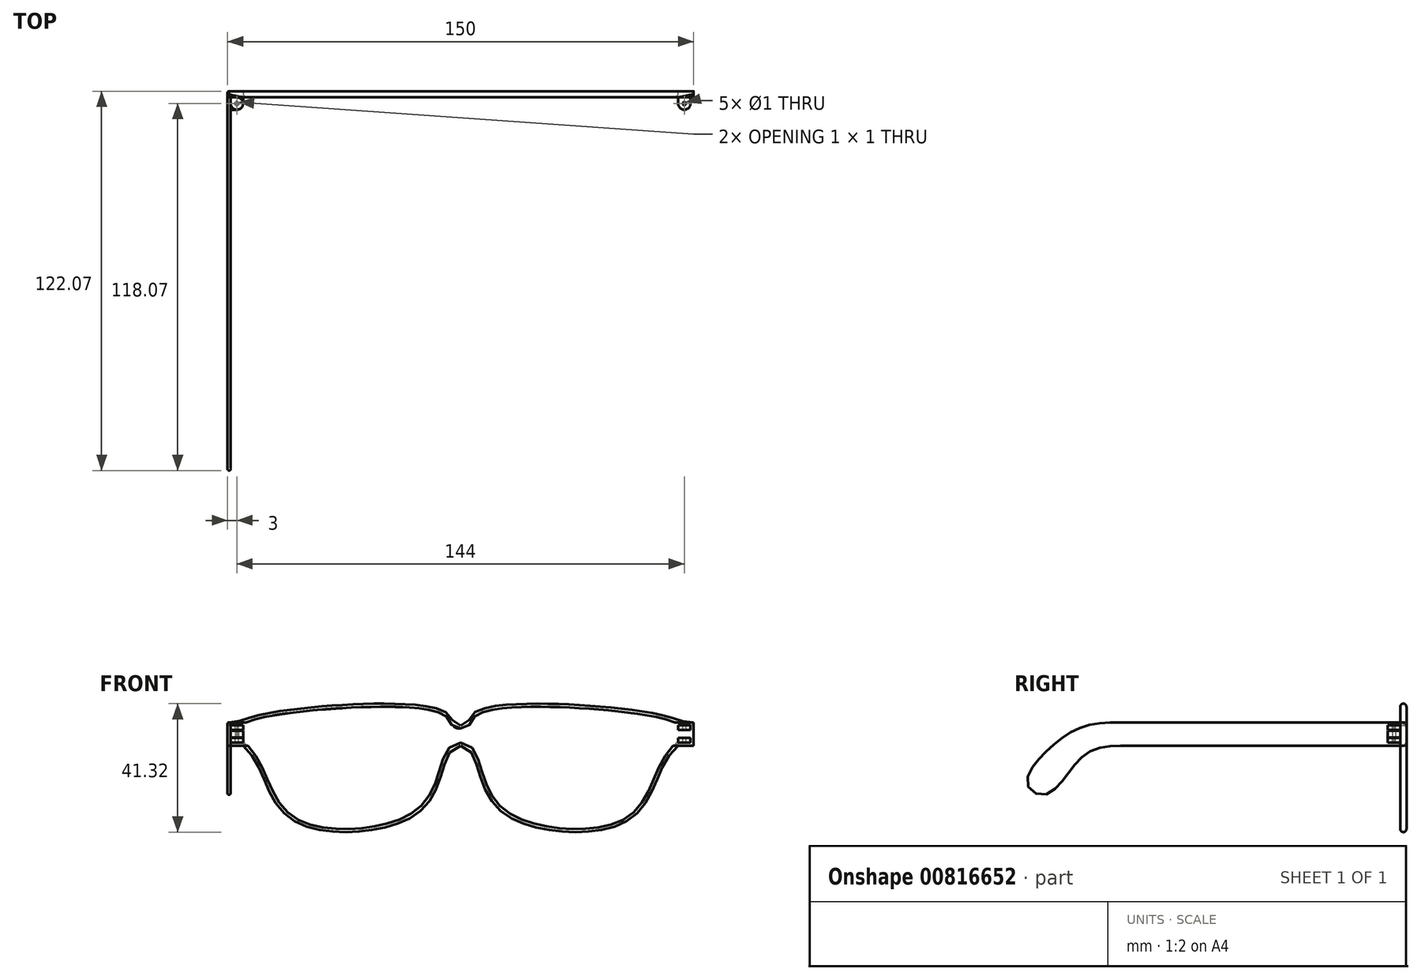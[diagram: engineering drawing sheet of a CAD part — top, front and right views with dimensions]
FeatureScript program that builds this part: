
annotation { "Feature Type Name" : "Feature", "Feature Type Description" : "" }
export const myFeature = defineFeature(function(context is Context, id is Id, definition is map)
    precondition{}
    {
        {
            var Q0;
            Q0=qCreatedBy(makeId("Front.planeOp"),FACE);
            var sketch = newSketch(context, id + "F0", { "sketchPlane" : qUnion([Q0])});
            skLineSegment(sketch, "E0", {"start": v(-75, -28.9) * mm, "end": v(-75, 32.7) * mm, "construction": true});
            skLineSegment(sketch, "E1", {"start": v(0, 0) * mm, "end": v(-4.56, 0) * mm, "construction": true});
            skLineSegment(sketch, "E2", {"start": v(-3.33, -24.15) * mm, "end": v(-65.98, -24.15) * mm, "construction": true});
            skLineSegment(sketch, "E3", {"start": v(-65.98, -24.15) * mm, "end": v(-64.31, 10) * mm, "construction": true});
            skLineSegment(sketch, "E4", {"start": v(-64.31, 10) * mm, "end": v(0, 10.78) * mm, "construction": true});
            skFitSpline(sketch, "E5", {"points": [v(0, 0) * mm, v(-4.25, -3.6) * mm, v(-7.5, -13.08) * mm, v(-18.05, -24.15) * mm, v(-53.68, -24.15) * mm, v(-65.12, -6.6) * mm, v(-69.95, 0) * mm, v(-75, 0) * mm], "startDerivative": vector(-72.74, 0) * mm, "endDerivative": vector(-133.49, 0) * mm});
            skFitSpline(sketch, "E6", {"points": [v(-75, 7.54) * mm, v(-64.31, 10) * mm, v(-4.56, 10.73) * mm, v(0, 6.53) * mm], "startDerivative": vector(58.2, 0) * mm, "endDerivative": vector(50.29, 0) * mm});
            skFitSpline(sketch, "E7.0", {"points": [v(-75, 4.04) * mm, v(-74.32, 4.04) * mm, v(-73.06, 4.09) * mm, v(-71.42, 4.29) * mm, v(-69.96, 4.62) * mm, v(-68.7, 5.01) * mm, v(-67.56, 5.41) * mm, v(-66.4, 5.81) * mm, v(-65.03, 6.23) * mm, v(-63.3, 6.66) * mm, v(-61.02, 7.11) * mm, v(-57.38, 7.72) * mm, v(-51.9, 8.44) * mm, v(-44.33, 9.2) * mm, v(-36.27, 9.76) * mm, v(-29.53, 10.02) * mm, v(-24.37, 10.06) * mm, v(-20.68, 10) * mm, v(-17.23, 9.86) * mm, v(-14.1, 9.61) * mm, v(-11.34, 9.26) * mm, v(-9.45, 8.9) * mm, v(-8.23, 8.56) * mm, v(-7.47, 8.3) * mm, v(-6.91, 8.07) * mm, v(-6.62, 7.9) * mm, v(-6.5, 7.82) * mm, v(-6.42, 7.75) * mm, v(-6.35, 7.67) * mm, v(-6.25, 7.54) * mm, v(-6.11, 7.31) * mm, v(-5.93, 6.95) * mm, v(-5.67, 6.43) * mm, v(-5.29, 5.75) * mm, v(-4.68, 4.92) * mm, v(-3.76, 4.07) * mm, v(-2.55, 3.42) * mm, v(-1.27, 3.09) * mm, v(-0.42, 3.03) * mm, v(0, 3.03) * mm]});
            skFitSpline(sketch, "E8.0", {"points": [v(0, 3.5) * mm, v(-0.65, 3.5) * mm, v(-1.95, 3.35) * mm, v(-3.73, 2.6) * mm, v(-5.14, 1.5) * mm, v(-6.17, 0.27) * mm, v(-6.78, -0.77) * mm, v(-7.2, -1.59) * mm, v(-7.46, -2.18) * mm, v(-7.7, -2.78) * mm, v(-8.02, -3.58) * mm, v(-8.37, -4.58) * mm, v(-8.75, -5.78) * mm, v(-9.24, -7.38) * mm, v(-9.85, -9.37) * mm, v(-10.67, -11.68) * mm, v(-11.65, -13.85) * mm, v(-12.88, -15.85) * mm, v(-14.45, -17.69) * mm, v(-16.16, -19.1) * mm, v(-17.87, -20.17) * mm, v(-19.1, -20.8) * mm, v(-20.2, -21.27) * mm, v(-21.36, -21.74) * mm, v(-22.96, -22.28) * mm, v(-25.04, -22.85) * mm, v(-28, -23.5) * mm, v(-31.98, -24.08) * mm, v(-36.9, -24.35) * mm, v(-40.92, -24.18) * mm, v(-43.96, -23.8) * mm, v(-46.11, -23.37) * mm, v(-48.11, -22.84) * mm, v(-49.91, -22.18) * mm, v(-51.23, -21.54) * mm, v(-52.16, -21) * mm, v(-53.03, -20.4) * mm, v(-54.01, -19.58) * mm, v(-55.44, -18.1) * mm, v(-56.97, -15.96) * mm, v(-58.51, -13) * mm, v(-59.65, -10.35) * mm, v(-60.56, -8.2) * mm, v(-61.14, -6.85) * mm, v(-61.62, -5.79) * mm, v(-62, -5) * mm, v(-62.4, -4.22) * mm, v(-62.95, -3.23) * mm, v(-63.64, -2.08) * mm, v(-64.48, -0.84) * mm, v(-65.3, 0.27) * mm, v(-65.97, 1.06) * mm, v(-66.5, 1.64) * mm, v(-66.9, 2.03) * mm, v(-67.32, 2.4) * mm, v(-67.76, 2.75) * mm, v(-68.26, 3.09) * mm, v(-68.95, 3.44) * mm, v(-69.78, 3.68) * mm, v(-70.55, 3.75) * mm, v(-71.12, 3.74) * mm, v(-71.56, 3.7) * mm, v(-71.94, 3.66) * mm, v(-72.47, 3.6) * mm, v(-73.32, 3.53) * mm, v(-74.36, 3.5) * mm, v(-75, 3.5) * mm]});
            skFitSpline(sketch, "E9", {"points": [v(-60.4, -8.59) * mm, v(-62.23, 5.12) * mm, v(-51.33, 8.47) * mm], "startDerivative": vector(-12.73, 32.46) * mm, "endDerivative": vector(25.15, 4.32) * mm});
            skLineSegment(sketch, "E10", {"start": v(0, 6.53) * mm, "end": v(0, 0) * mm});
            skLineSegment(sketch, "E11", {"start": v(-75, 7.54) * mm, "end": v(-75, 0) * mm});
            skPoint(sketch, "E12.2.internal.snap0", {"position": v(-65.14, -7.08) * mm});
            skFitSpline(sketch, "E12", {"points": [v(-13.23, 9.5) * mm, v(-8.44, 6.53) * mm, v(-9.15, -7.08) * mm], "startDerivative": vector(14.77, -3.56) * mm, "endDerivative": vector(-7.02, -20.16) * mm});
            skLineSegment(sketch, "E13", {"start": v(-7.5, -22.45) * mm, "end": v(-7.5, 12.5) * mm, "construction": true});
            skSolve(sketch);
        }
        {
            var Q0;
            {var subQ8=sQuery(id+"F0.wireOp",EDGE,"E6");Q0=makeQuery(id+"F0.imprint","IMPRINT",FACE,{"disambiguationData":[TD([[makeQuery(id+"F0.imprint","IMPRINT",EDGE,{"derivedFrom":subQ8}),-1.0]])]});}
            var Q1;
            {var subQ3=sQuery(id+"F0.wireOp",EDGE,"E9");Q1=makeQuery(id+"F0.imprint","IMPRINT",FACE,{"disambiguationData":[TD([[makeQuery(id+"F0.imprint","IMPRINT",EDGE,{"derivedFrom":subQ3}),1.0]])]});}
            var Q2;
            {var subQ7=sQuery(id+"F0.wireOp",EDGE,"E5");Q2=makeQuery(id+"F0.imprint","IMPRINT",FACE,{"disambiguationData":[TD([[makeQuery(id+"F0.imprint","IMPRINT",EDGE,{"derivedFrom":subQ7}),-1.0]])]});}
            var Q3;
            {var subQ0=sQuery(id+"F0.wireOp",EDGE,"E10");var subQ1=sQuery(id+"F0.wireOp",EDGE,"E7.0");var subQ2=makeQuery(id+"F0.imprint","INTERSECT",VERTEX,{"derivedFrom":[subQ1,subQ0]});Q3=makeQuery(id+"F0.imprint","IMPRINT",FACE,{"disambiguationData":[TD([[makeQuery(id+"F0.imprint","IMPRINT",EDGE,{"disambiguationData":[TD([[subQ2,1.0]])],"derivedFrom":subQ1}),-1.0]])]});}
            var Q4;
            {var subQ0=sQuery(id+"F0.wireOp",EDGE,"E12");var subQ1=sQuery(id+"F0.wireOp",EDGE,"E7.0");var subQ2=makeQuery(id+"F0.imprint","INTERSECT",VERTEX,{"disambiguationData":[OD(1.0)],"derivedFrom":[subQ1,subQ0]});Q4=makeQuery(id+"F0.imprint","IMPRINT",FACE,{"disambiguationData":[TD([[makeQuery(id+"F0.imprint","IMPRINT",EDGE,{"disambiguationData":[TD([[subQ2,-1.0]])],"derivedFrom":subQ1}),-1.0]])]});}
            var Q5;
            {var subQ0=sQuery(id+"F0.wireOp",EDGE,"E10");var subQ1=sQuery(id+"F0.wireOp",EDGE,"E7.0");var subQ2=makeQuery(id+"F0.imprint","INTERSECT",VERTEX,{"derivedFrom":[subQ1,subQ0]});Q5=makeQuery(id+"F0.imprint","IMPRINT",FACE,{"disambiguationData":[TD([[makeQuery(id+"F0.imprint","IMPRINT",EDGE,{"disambiguationData":[TD([[subQ2,1.0]])],"derivedFrom":subQ1}),1.0]])]});}
            extrude(context, id + "F1", {"entities" : qUnion([Q0, Q1, Q2, Q3, Q4, Q5]), "depth" : 2 * mm, "offsetDistance" : 25 * mm});
        }
        {
            var Q0;
            Q0=makeQuery(id+"F1.opExtrude","CAP_EDGE",EDGE,{"disambiguationData":[OSD([sQuery(id+"F0.wireOp",EDGE,"E5")])],"isStart":false});
            var Q1;
            Q1=makeQuery(id+"F1.opExtrude","CAP_EDGE",EDGE,{"disambiguationData":[OSD([sQuery(id+"F0.wireOp",EDGE,"E6")])],"isStart":false});
            var Q2;
            Q2=makeQuery(id+"F1.opExtrude","CAP_EDGE",EDGE,{"disambiguationData":[OSD([sQuery(id+"F0.wireOp",EDGE,"E5")])],"isStart":true});
            var Q3;
            Q3=makeQuery(id+"F1.opExtrude","CAP_EDGE",EDGE,{"disambiguationData":[OSD([sQuery(id+"F0.wireOp",EDGE,"E6")])],"isStart":true});
            fillet(context, id + "F2", {"entities" : qUnion([Q0, Q1, Q2, Q3]), "radius" : 1 * mm, "tangentPropagation" : true, "allowEdgeOverflow" : false});
        }
        {
            var Q0;
            Q0=makeQuery(id+"F1.opExtrude","SWEPT_FACE",FACE,{"disambiguationData":[OSD([sQuery(id+"F0.wireOp",EDGE,"E11")])]});
            var sketch = newSketch(context, id + "F3", { "sketchPlane" : qUnion([Q0])});
            skLineSegment(sketch, "E14", {"start": v(1, 7.54) * mm, "end": v(1, 0) * mm});
            skLineSegment(sketch, "E15", {"start": v(1, 0) * mm, "end": v(7.33, 0) * mm});
            skLineSegment(sketch, "E16", {"start": v(7.33, 0) * mm, "end": v(7.33, 7.54) * mm});
            skLineSegment(sketch, "E17", {"start": v(7.33, 7.54) * mm, "end": v(1, 7.54) * mm});
            skSolve(sketch);
        }
        {
            var Q0;
            Q0=makeQuery(id+"F3.imprint","IMPRINT",FACE,{"disambiguationData":[TD([[makeQuery(id+"F3.imprint","IMPRINT",EDGE,{"derivedFrom":sQuery(id+"F3.wireOp",EDGE,"E14")}),-1.0]])]});
            var Q1;
            Q1=makeQuery(id+"F3.imprint","IMPRINT",FACE,{"disambiguationData":[TD([[makeQuery(id+"F3.imprint","IMPRINT",EDGE,{"derivedFrom":sQuery(id+"F3.wireOp",EDGE,"E14")}),1.0]])]});
            var Q2;
            Q2=makeQuery(id+"F3.imprint","IMPRINT",FACE,{"disambiguationData":[TD([[makeQuery(id+"F3.imprint","IMPRINT",EDGE,{"derivedFrom":sQuery(id+"F3.wireOp",EDGE,"E15")}),1.0]])]});
            extrude(context, id + "F4", {"entities" : qUnion([Q0, Q1, Q2]), "operationType" : NewBodyOperationType.ADD, "oppositeDirection" : true, "depth" : 10 * mm, "offsetDistance" : 25 * mm});
        }
        {
            var Q0;
            Q0=makeQuery(id+"F4.opExtrude","SWEPT_FACE",FACE,{"disambiguationData":[OSD([sQuery(id+"F3.wireOp",EDGE,"E17")])]});
            var sketch = newSketch(context, id + "F5", { "sketchPlane" : qUnion([Q0])});
            skLineSegment(sketch, "E18", {"start": v(-65, -2) * mm, "end": v(-75, -2) * mm, "construction": true});
            skLineSegment(sketch, "E19", {"start": v(-75, -2) * mm, "end": v(-74, -2) * mm});
            skLineSegment(sketch, "E20", {"start": v(-74, -2) * mm, "end": v(-74, -4) * mm});
            skLineSegment(sketch, "E21", {"start": v(-74, -4) * mm, "end": v(-72, -4) * mm, "construction": true});
            skArc(sketch, "E22", {"start": v(-74, -4) * mm, "mid": v(-72, -6) * mm, "end": v(-70, -4) * mm});
            skLineSegment(sketch, "E23", {"start": v(-70, -4) * mm, "end": v(-70, -2) * mm});
            skCircle(sketch, "E24", {"center": v(-72, -4) * mm, "radius": 0.5 * mm});
            skLineSegment(sketch, "E25", {"start": v(-70, -2) * mm, "end": v(-69.05, -2) * mm});
            skSolve(sketch);
        }
        {
            var Q0;
            {var subQ8=sQuery(id+"F5.wireOp",EDGE,"E19");Q0=makeQuery(id+"F5.imprint","IMPRINT",FACE,{"disambiguationData":[TD([[makeQuery(id+"F5.imprint","IMPRINT",EDGE,{"derivedFrom":subQ8}),-1.0]])]});}
            var Q1;
            Q1=makeQuery(id+"F5.imprint","IMPRINT",FACE,{"disambiguationData":[TD([[makeQuery(id+"F5.imprint","IMPRINT",EDGE,{"derivedFrom":sQuery(id+"F5.wireOp",EDGE,"E24")}),1.0]])]});
            extrude(context, id + "F6", {"entities" : qUnion([Q0, Q1]), "operationType" : NewBodyOperationType.REMOVE, "oppositeDirection" : true, "depth" : 25 * mm, "offsetDistance" : 25 * mm});
        }
        {
            var Q0;
            Q0=makeQuery(id+"F6.boolean.opBoolean","COPY",FACE,{"derivedFrom":makeQuery(id+"F6.opExtrude","SWEPT_FACE",FACE,{"disambiguationData":[OSD([sQuery(id+"F5.wireOp",EDGE,"E20")])]})});
            var sketch = newSketch(context, id + "F7", { "sketchPlane" : qUnion([Q0])});
            skLineSegment(sketch, "E26", {"start": v(2, 7.54) * mm, "end": v(2, 6.54) * mm});
            skLineSegment(sketch, "E27", {"start": v(2, 6.54) * mm, "end": v(6.7, 6.54) * mm});
            skLineSegment(sketch, "E28", {"start": v(6.7, 6.54) * mm, "end": v(6.7, 5.04) * mm});
            skLineSegment(sketch, "E29", {"start": v(6.7, 5.04) * mm, "end": v(2, 5.04) * mm});
            skLineSegment(sketch, "E30", {"start": v(2, 5.04) * mm, "end": v(2, 2.5) * mm});
            skLineSegment(sketch, "E31", {"start": v(2, 2.5) * mm, "end": v(6.7, 2.5) * mm});
            skLineSegment(sketch, "E32", {"start": v(6.7, 2.5) * mm, "end": v(6.7, 1) * mm});
            skLineSegment(sketch, "E33", {"start": v(6.7, 1) * mm, "end": v(2, 1) * mm});
            skLineSegment(sketch, "E34", {"start": v(2, 1) * mm, "end": v(2, 0) * mm});
            skLineSegment(sketch, "E35", {"start": v(2, 7.54) * mm, "end": v(6.7, 7.54) * mm});
            skLineSegment(sketch, "E36", {"start": v(6.7, 7.54) * mm, "end": v(6.7, 6.54) * mm});
            skLineSegment(sketch, "E37", {"start": v(6.7, 5.04) * mm, "end": v(6.7, 2.5) * mm});
            skLineSegment(sketch, "E38", {"start": v(6.7, 1) * mm, "end": v(6.7, 0) * mm});
            skLineSegment(sketch, "E39", {"start": v(6.7, 0) * mm, "end": v(2, 0) * mm});
            skLineSegment(sketch, "E40", {"start": v(2, 1) * mm, "end": v(2, 2.5) * mm});
            skLineSegment(sketch, "E41", {"start": v(2, 5.04) * mm, "end": v(2, 6.54) * mm});
            skSolve(sketch);
        }
        {
            var Q0;
            {var subQ0=sQuery(id+"F7.wireOp",EDGE,"E36");Q0=makeQuery(id+"F7.imprint","IMPRINT",FACE,{"disambiguationData":[TD([[makeQuery(id+"F7.imprint","IMPRINT",EDGE,{"derivedFrom":subQ0}),-1.0]])]});}
            var Q1;
            {var subQ0=sQuery(id+"F7.wireOp",EDGE,"E26");Q1=makeQuery(id+"F7.imprint","IMPRINT",FACE,{"disambiguationData":[TD([[makeQuery(id+"F7.imprint","IMPRINT",EDGE,{"derivedFrom":subQ0}),-1.0]])]});}
            var Q2;
            {var subQ0=sQuery(id+"F7.wireOp",EDGE,"E30");Q2=makeQuery(id+"F7.imprint","IMPRINT",FACE,{"disambiguationData":[TD([[makeQuery(id+"F7.imprint","IMPRINT",EDGE,{"derivedFrom":subQ0}),-1.0]])]});}
            var Q3;
            {var subQ0=sQuery(id+"F7.wireOp",EDGE,"E37");Q3=makeQuery(id+"F7.imprint","IMPRINT",FACE,{"disambiguationData":[TD([[makeQuery(id+"F7.imprint","IMPRINT",EDGE,{"derivedFrom":subQ0}),-1.0]])]});}
            var Q4;
            {var subQ0=sQuery(id+"F7.wireOp",EDGE,"E38");Q4=makeQuery(id+"F7.imprint","IMPRINT",FACE,{"disambiguationData":[TD([[makeQuery(id+"F7.imprint","IMPRINT",EDGE,{"derivedFrom":subQ0}),-1.0]])]});}
            var Q5;
            {var subQ0=sQuery(id+"F7.wireOp",EDGE,"E34");Q5=makeQuery(id+"F7.imprint","IMPRINT",FACE,{"disambiguationData":[TD([[makeQuery(id+"F7.imprint","IMPRINT",EDGE,{"derivedFrom":subQ0}),-1.0]])]});}
            extrude(context, id + "F8", {"entities" : qUnion([Q0, Q1, Q2, Q3, Q4, Q5]), "operationType" : NewBodyOperationType.REMOVE, "oppositeDirection" : true, "depth" : 25 * mm, "offsetDistance" : 25 * mm});
        }
        {
            var Q0;
            {var subQ0=sQuery(id+"F0.wireOp",EDGE,"E11");Q0=makeQuery(id+"F4.boolean.opBoolean","MERGE",FACE,{"derivedFrom":[makeQuery(id+"F1.opExtrude","SWEPT_FACE",FACE,{"disambiguationData":[OSD([subQ0])]}),makeQuery(id+"F4.opExtrude","CAP_FACE",FACE,{"disambiguationData":[OSD([sQuery(id+"F0.wireOp",EDGE,"E5"),sQuery(id+"F0.wireOp",EDGE,"E6"),subQ0,sQuery(id+"F3.wireOp",EDGE,"E15"),sQuery(id+"F3.wireOp",EDGE,"E16"),sQuery(id+"F3.wireOp",EDGE,"E17")])],"isStart":true})]});}
            var sketch = newSketch(context, id + "F9", { "sketchPlane" : qUnion([Q0])});
            skLineSegment(sketch, "E42", {"start": v(2, 7.54) * mm, "end": v(2, 0) * mm});
            skLineSegment(sketch, "E43", {"start": v(2, 0) * mm, "end": v(92, 0) * mm});
            skLineSegment(sketch, "E44", {"start": v(92, 7.54) * mm, "end": v(2, 7.54) * mm});
            skFitSpline(sketch, "E45", {"points": [v(92, 0) * mm, v(104.49, -3.74) * mm, v(115.9, -15.6) * mm, v(122.04, -11.92) * mm, v(109.95, 3.06) * mm, v(92, 7.54) * mm], "startDerivative": vector(78.78, 0) * mm, "endDerivative": vector(-118.5, 0) * mm});
            skSolve(sketch);
        }
        {
            var Q0;
            Q0=makeQuery(id+"F9.imprint","IMPRINT",FACE,{"disambiguationData":[TD([[makeQuery(id+"F9.imprint","IMPRINT",EDGE,{"derivedFrom":sQuery(id+"F9.wireOp",EDGE,"E42")}),-1.0]])]});
            extrude(context, id + "F10", {"entities" : qUnion([Q0]), "oppositeDirection" : true, "depth" : 1 * mm, "offsetDistance" : 25 * mm});
        }
        {
            var Q0;
            {var subQ0=sQuery(id+"F0.wireOp",EDGE,"E5");Q0=makeQuery(id+"F2.opFillet","BLEND_EDGE",EDGE,{"blendedFrom":[makeQuery(id+"F1.opExtrude","CAP_EDGE",EDGE,{"disambiguationData":[OSD([subQ0])],"isStart":true}),makeQuery(id+"F1.opExtrude","CAP_EDGE",EDGE,{"disambiguationData":[OSD([subQ0])],"isStart":false})],"blendedInto":[]});}
            cPoint(context, id + "F11", {"entities" : qUnion([Q0]), "parameter" : 0.5});
        }
        {
            var Q0;
            {var subQ0=sQuery(id+"F0.wireOp",EDGE,"E5");var subQ1=makeQuery(id+"F2.opFillet","BLEND_VERTEX",VERTEX,{"blendedFrom":[makeQuery(id+"F1.opExtrude","CAP_EDGE",EDGE,{"disambiguationData":[OSD([subQ0])],"isStart":true}),makeQuery(id+"F1.opExtrude","CAP_EDGE",EDGE,{"disambiguationData":[OSD([subQ0])],"isStart":false}),makeQuery(id+"F1.opExtrude","SWEPT_FACE",FACE,{"disambiguationData":[OSD([sQuery(id+"F0.wireOp",EDGE,"E10")])]})],"blendedInto":[makeQuery(id+"F1.opExtrude","SWEPT_FACE",FACE,{"disambiguationData":[OSD([sQuery(id+"F0.wireOp",EDGE,"E10")])]})]});Q0=makeQuery(id+"F13.boolean.opBoolean","MERGE",VERTEX,{"derivedFrom":[subQ1,makeQuery(id+"F13.opPattern","COPY",VERTEX,{"derivedFrom":subQ1,"instanceName":"1"})]});}
            var Q1;
            Q1 = qCreatedBy(id + "F11" ,VERTEX);
            var Q2;
            {var subQ0=sQuery(id+"F0.wireOp",EDGE,"E5");Q2=makeQuery(id+"F4.boolean.opBoolean","INTERSECT",VERTEX,{"derivedFrom":[makeQuery(id+"F2.opFillet","BLEND_FACE",FACE,{"disambiguationData":[OSD([subQ0]),TDD([makeQuery(id+"F1.opExtrude","CAP_EDGE",EDGE,{"disambiguationData":[OSD([subQ0])],"isStart":true})])]}),makeQuery(id+"F2.opFillet","BLEND_FACE",FACE,{"disambiguationData":[OSD([subQ0]),TDD([makeQuery(id+"F1.opExtrude","CAP_EDGE",EDGE,{"disambiguationData":[OSD([subQ0])],"isStart":false})])]}),makeQuery(id+"F4.opExtrude","SWEPT_FACE",FACE,{"disambiguationData":[OSD([sQuery(id+"F3.wireOp",EDGE,"E15")])]}),makeQuery(id+"F4.opExtrude","SWEPT_FACE",FACE,{"disambiguationData":[OSD([subQ0,sQuery(id+"F0.wireOp",EDGE,"E11")])]})]});}
            cPlane(context, id + "F12", {"entities" : qUnion([Q0, Q1, Q2]), "cplaneType" : CPlaneType.THREE_POINT, "offset" : 25 * mm, "width" : 150 * mm, "height" : 150 * mm});
        }
        {
            var Q0;
            Q0=makeQuery(id+"F1.opExtrude","SWEPT_BODY",BODY,{"disambiguationData":[OSD([sQuery(id+"F0.wireOp",EDGE,"E5"),sQuery(id+"F0.wireOp",EDGE,"E6"),sQuery(id+"F0.wireOp",EDGE,"E7.0"),sQuery(id+"F0.wireOp",EDGE,"E8.0"),sQuery(id+"F0.wireOp",EDGE,"E9"),sQuery(id+"F0.wireOp",EDGE,"5d8ac839-612c-406b-9722-8f7b15ceff4e"),sQuery(id+"F0.wireOp",EDGE,"E10"),sQuery(id+"F0.wireOp",EDGE,"E11")])]});
            var Q1;
            Q1=makeQuery(id+"F1.opExtrude","SWEPT_FACE",FACE,{"disambiguationData":[OSD([sQuery(id+"F0.wireOp",EDGE,"E10")])]});
            mirror(context, id + "F13", {"operationType" : NewBodyOperationType.ADD, "entities" : qUnion([Q0]), "mirrorPlane" : qUnion([Q1])});
        }
        {
            var Q0;
            Q0=makeQuery(id+"F10.opExtrude","CAP_EDGE",EDGE,{"disambiguationData":[OSD([sQuery(id+"F9.wireOp",EDGE,"E43")])],"isStart":true});
            var Q1;
            Q1=makeQuery(id+"F10.opExtrude","CAP_EDGE",EDGE,{"disambiguationData":[OSD([sQuery(id+"F9.wireOp",EDGE,"E43")])],"isStart":false});
            var Q2;
            Q2=makeQuery(id+"F10.opExtrude","CAP_EDGE",EDGE,{"disambiguationData":[OSD([sQuery(id+"F9.wireOp",EDGE,"E44")])],"isStart":false});
            var Q3;
            Q3=makeQuery(id+"F10.opExtrude","CAP_EDGE",EDGE,{"disambiguationData":[OSD([sQuery(id+"F9.wireOp",EDGE,"E45")])],"isStart":false});
            var Q4;
            Q4=makeQuery(id+"F10.opExtrude","CAP_EDGE",EDGE,{"disambiguationData":[OSD([sQuery(id+"F9.wireOp",EDGE,"E45")])],"isStart":true});
            var Q5;
            Q5=makeQuery(id+"F10.opExtrude","CAP_EDGE",EDGE,{"disambiguationData":[OSD([sQuery(id+"F9.wireOp",EDGE,"E44")])],"isStart":true});
            fillet(context, id + "F14", {"entities" : qUnion([Q0, Q1, Q2, Q3, Q4, Q5]), "radius" : 0.5 * mm, "tangentPropagation" : true, "allowEdgeOverflow" : false});
        }
        {
            var Q0;
            Q0=makeQuery(id+"F10.opExtrude","CAP_FACE",FACE,{"disambiguationData":[OSD([sQuery(id+"F9.wireOp",EDGE,"E42"),sQuery(id+"F9.wireOp",EDGE,"E43"),sQuery(id+"F9.wireOp",EDGE,"E44"),sQuery(id+"F9.wireOp",EDGE,"E45")])],"isStart":false});
            var sketch = newSketch(context, id + "F15", { "sketchPlane" : qUnion([Q0])});
            skPoint(sketch, "E46.0", {"position": v(-6, 5.04) * mm});
            skPoint(sketch, "E47.0", {"position": v(-6, 2.5) * mm});
            skLineSegment(sketch, "E48", {"start": v(-2, 4.84) * mm, "end": v(-6, 4.84) * mm});
            skLineSegment(sketch, "E49", {"start": v(-6, 4.84) * mm, "end": v(-6, 2.7) * mm});
            skLineSegment(sketch, "E50", {"start": v(-6, 2.7) * mm, "end": v(-2, 2.7) * mm});
            skLineSegment(sketch, "E51", {"start": v(-2, 2.7) * mm, "end": v(-2, 4.84) * mm});
            skSolve(sketch);
        }
        {
            var Q0;
            Q0=makeQuery(id+"F15.imprint","IMPRINT",FACE,{"disambiguationData":[TD([[makeQuery(id+"F15.imprint","IMPRINT",EDGE,{"derivedFrom":sQuery(id+"F15.wireOp",EDGE,"E48")}),1.0]])]});
            extrude(context, id + "F16", {"entities" : qUnion([Q0]), "operationType" : NewBodyOperationType.ADD, "depth" : 4 * mm, "offsetDistance" : 25 * mm});
        }
        {
            var Q0;
            Q0=makeQuery(id+"F16.opExtrude","SWEPT_FACE",FACE,{"disambiguationData":[OSD([sQuery(id+"F15.wireOp",EDGE,"E50")])]});
            var sketch = newSketch(context, id + "F17", { "sketchPlane" : qUnion([Q0])});
            skLineSegment(sketch, "E52", {"start": v(-70, 2) * mm, "end": v(-70, 4) * mm, "construction": true});
            skLineSegment(sketch, "E53", {"start": v(-70, 4) * mm, "end": v(-72, 4) * mm, "construction": true});
            skArc(sketch, "E54", {"start": v(-72, 2) * mm, "mid": v(-70, 4) * mm, "end": v(-72, 6) * mm});
            skCircle(sketch, "E55", {"center": v(-72, 4) * mm, "radius": 0.5 * mm});
            skSolve(sketch);
        }
        {
            var Q0;
            Q0=makeQuery(id+"F17.imprint","IMPRINT",FACE,{"disambiguationData":[TD([[makeQuery(id+"F17.imprint","IMPRINT",EDGE,{"derivedFrom":sQuery(id+"F17.wireOp",EDGE,"E55")}),1.0]])]});
            var Q1;
            {var subQ0=sQuery(id+"F17.wireOp",EDGE,"E54");var subQ1=sQuery(id+"F15.wireOp",EDGE,"E50");var subQ4=makeQuery(id+"F16.opExtrude","CAP_EDGE",EDGE,{"disambiguationData":[OSD([subQ1])],"isStart":false});var subQ5=makeQuery(id+"F17.imprint","INTERSECT",VERTEX,{"derivedFrom":[subQ4,subQ0]});Q1=makeQuery(id+"F17.imprint","IMPRINT",FACE,{"disambiguationData":[TD([[makeQuery(id+"F17.imprint","IMPRINT",EDGE,{"disambiguationData":[TD([[subQ5,1.0]])],"derivedFrom":subQ0}),-1.0]])]});}
            var Q2;
            {var subQ0=sQuery(id+"F17.wireOp",EDGE,"E54");var subQ1=sQuery(id+"F15.wireOp",EDGE,"E50");var subQ4=makeQuery(id+"F16.opExtrude","CAP_EDGE",EDGE,{"disambiguationData":[OSD([subQ1])],"isStart":false});var subQ5=makeQuery(id+"F17.imprint","INTERSECT",VERTEX,{"derivedFrom":[subQ4,subQ0]});Q2=makeQuery(id+"F17.imprint","IMPRINT",FACE,{"disambiguationData":[TD([[makeQuery(id+"F17.imprint","IMPRINT",EDGE,{"disambiguationData":[TD([[subQ5,-1.0]])],"derivedFrom":subQ0}),-1.0]])]});}
            extrude(context, id + "F18", {"entities" : qUnion([Q0, Q1, Q2]), "operationType" : NewBodyOperationType.REMOVE, "oppositeDirection" : true, "depth" : 25 * mm, "offsetDistance" : 25 * mm});
        }
    });
